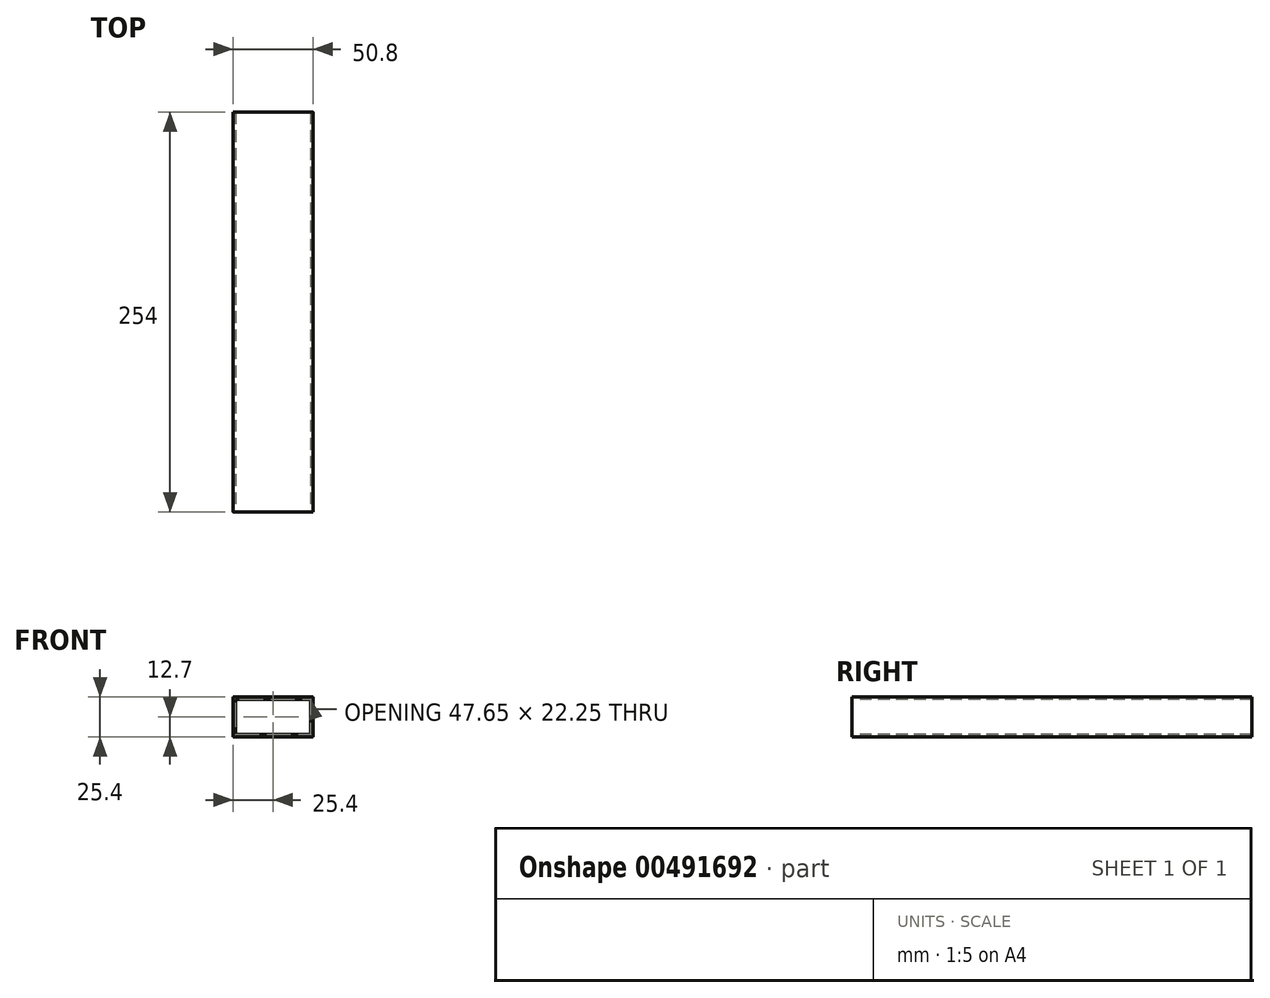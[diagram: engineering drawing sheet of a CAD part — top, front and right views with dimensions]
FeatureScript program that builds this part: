
annotation { "Feature Type Name" : "Feature", "Feature Type Description" : "" }
export const myFeature = defineFeature(function(context is Context, id is Id, definition is map)
    precondition{}
    {
        {
            var Q0;
            Q0=qCreatedBy(makeId("Front.planeOp"),FACE);
            var sketch = newSketch(context, id + "F0", { "sketchPlane" : qUnion([Q0])});
            skLineSegment(sketch, "E0.bottom", {"start": v(25.4, 12.7) * mm, "end": v(-25.4, 12.7) * mm});
            skLineSegment(sketch, "E0.top", {"start": v(25.4, -12.7) * mm, "end": v(-25.4, -12.7) * mm});
            skLineSegment(sketch, "E0.left", {"start": v(25.4, 12.7) * mm, "end": v(25.4, -12.7) * mm});
            skLineSegment(sketch, "E0.right", {"start": v(-25.4, 12.7) * mm, "end": v(-25.4, -12.7) * mm});
            skPoint(sketch, "E0.middle", {"position": v(0, 0) * mm});
            skSolve(sketch);
        }
        {
            var Q0;
            Q0 = qSketchRegion(id + "F0", true);
            extrude(context, id + "F1", {"entities" : qUnion([Q0]), "depth" : 254 * mm});
        }
        {
            var Q0;
            Q0=makeQuery(id+"F1.opExtrude","CAP_FACE",FACE,{"disambiguationData":[OSD([sQuery(id+"F0.wireOp",EDGE,"E0.bottom"),sQuery(id+"F0.wireOp",EDGE,"E0.top"),sQuery(id+"F0.wireOp",EDGE,"E0.left"),sQuery(id+"F0.wireOp",EDGE,"E0.right")])],"isStart":false});
            var sketch = newSketch(context, id + "F2", { "sketchPlane" : qUnion([Q0])});
            skLineSegment(sketch, "E1.bottom", {"start": v(23.83, 11.13) * mm, "end": v(-23.83, 11.13) * mm});
            skLineSegment(sketch, "E1.top", {"start": v(23.83, -11.13) * mm, "end": v(-23.83, -11.13) * mm});
            skLineSegment(sketch, "E1.left", {"start": v(23.83, 11.13) * mm, "end": v(23.83, -11.13) * mm});
            skLineSegment(sketch, "E1.right", {"start": v(-23.83, 11.13) * mm, "end": v(-23.83, -11.13) * mm});
            skPoint(sketch, "E1.middle", {"position": v(0, 0) * mm});
            skSolve(sketch);
        }
        {
            var Q0;
            Q0 = qSketchRegion(id + "F2", true);
            extrude(context, id + "F3", {"entities" : qUnion([Q0]), "operationType" : NewBodyOperationType.REMOVE, "endBound" : BoundingType.UP_TO_NEXT, "oppositeDirection" : true, "depth" : 25.4 * mm});
        }
        {
            var Q0;
            Q0=makeQuery(id+"F3.boolean.opBoolean","COPY",EDGE,{"derivedFrom":makeQuery(id+"F3.opExtrude","SWEPT_EDGE",EDGE,{"disambiguationData":[OSD([sQuery(id+"F2.wireOp",EDGE,"E1.top"),sQuery(id+"F2.wireOp",EDGE,"E1.left")])]})});
            var Q1;
            Q1=makeQuery(id+"F3.boolean.opBoolean","COPY",EDGE,{"derivedFrom":makeQuery(id+"F3.opExtrude","SWEPT_EDGE",EDGE,{"disambiguationData":[OSD([sQuery(id+"F2.wireOp",EDGE,"E1.bottom"),sQuery(id+"F2.wireOp",EDGE,"E1.left")])]})});
            var Q2;
            Q2=makeQuery(id+"F3.boolean.opBoolean","COPY",EDGE,{"derivedFrom":makeQuery(id+"F3.opExtrude","SWEPT_EDGE",EDGE,{"disambiguationData":[OSD([sQuery(id+"F2.wireOp",EDGE,"E1.top"),sQuery(id+"F2.wireOp",EDGE,"E1.right")])]})});
            var Q3;
            Q3=makeQuery(id+"F3.boolean.opBoolean","COPY",EDGE,{"derivedFrom":makeQuery(id+"F3.opExtrude","SWEPT_EDGE",EDGE,{"disambiguationData":[OSD([sQuery(id+"F2.wireOp",EDGE,"E1.bottom"),sQuery(id+"F2.wireOp",EDGE,"E1.right")])]})});
            fillet(context, id + "F4", {"entities" : qUnion([Q0, Q1, Q2, Q3]), "radius" : 1.52 * mm, "tangentPropagation" : true, "allowEdgeOverflow" : false});
        }
        {
            var Q0;
            Q0=makeQuery(id+"F1.opExtrude","SWEPT_EDGE",EDGE,{"disambiguationData":[OSD([sQuery(id+"F0.wireOp",EDGE,"E0.bottom"),sQuery(id+"F0.wireOp",EDGE,"E0.right")])]});
            var Q1;
            Q1=makeQuery(id+"F1.opExtrude","SWEPT_EDGE",EDGE,{"disambiguationData":[OSD([sQuery(id+"F0.wireOp",EDGE,"E0.bottom"),sQuery(id+"F0.wireOp",EDGE,"E0.left")])]});
            var Q2;
            Q2=makeQuery(id+"F1.opExtrude","SWEPT_EDGE",EDGE,{"disambiguationData":[OSD([sQuery(id+"F0.wireOp",EDGE,"E0.top"),sQuery(id+"F0.wireOp",EDGE,"E0.left")])]});
            var Q3;
            Q3=makeQuery(id+"F1.opExtrude","SWEPT_EDGE",EDGE,{"disambiguationData":[OSD([sQuery(id+"F0.wireOp",EDGE,"E0.top"),sQuery(id+"F0.wireOp",EDGE,"E0.right")])]});
            fillet(context, id + "F5", {"entities" : qUnion([Q0, Q1, Q2, Q3]), "radius" : 0.25 * mm, "tangentPropagation" : true, "allowEdgeOverflow" : false});
        }
    });
